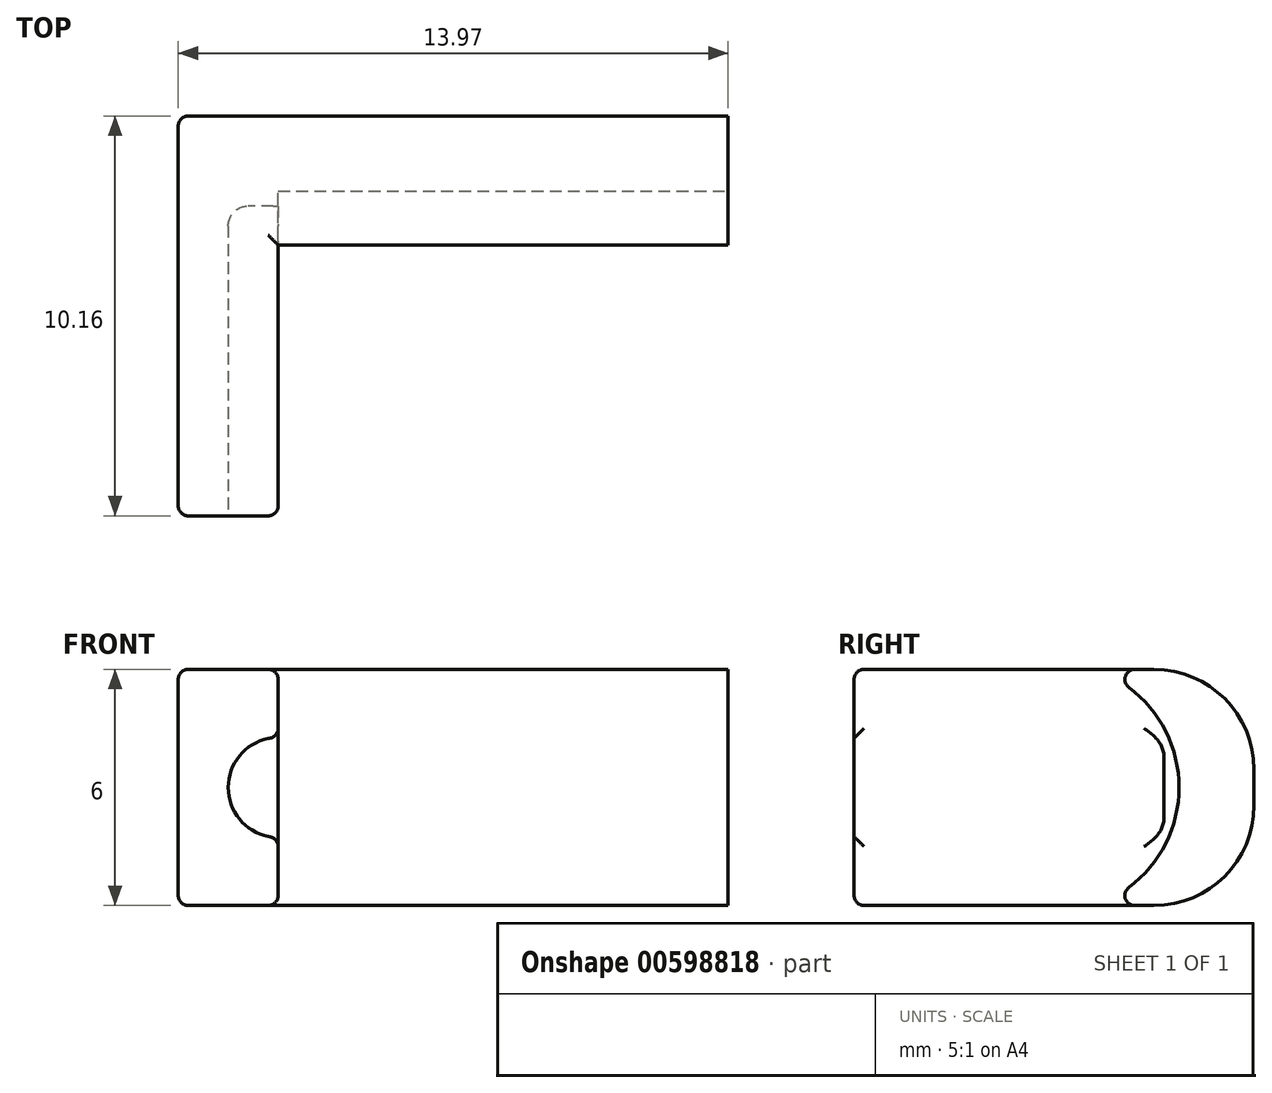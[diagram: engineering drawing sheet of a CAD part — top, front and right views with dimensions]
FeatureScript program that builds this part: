
annotation { "Feature Type Name" : "Feature", "Feature Type Description" : "" }
export const myFeature = defineFeature(function(context is Context, id is Id, definition is map)
    precondition{}
    {
        {
            var Q0;
            Q0=qCreatedBy(makeId("Top.planeOp"),FACE);
            var sketch = newSketch(context, id + "F0", { "sketchPlane" : qUnion([Q0])});
            skLineSegment(sketch, "E0", {"start": v(0, 0) * mm, "end": v(0, 0) * mm});
            skLineSegment(sketch, "E1.bottom", {"start": v(0, 0) * mm, "end": v(-13.97, 0) * mm});
            skLineSegment(sketch, "E1.top", {"start": v(0, -5.08) * mm, "end": v(-13.97, -5.08) * mm});
            skLineSegment(sketch, "E1.left", {"start": v(0, 0) * mm, "end": v(0, -5.08) * mm});
            skLineSegment(sketch, "E1.right", {"start": v(-13.97, 0) * mm, "end": v(-13.97, -5.08) * mm});
            skSolve(sketch);
        }
        {
            var Q0;
            Q0 = qSketchRegion(id + "F0", true);
            extrude(context, id + "F1", {"entities" : qUnion([Q0]), "depth" : 6 * mm, "offsetDistance" : 25.4 * mm});
        }
        {
            var Q0;
            Q0=makeQuery(id+"F1.opExtrude","SWEPT_FACE",FACE,{"disambiguationData":[OSD([sQuery(id+"F0.wireOp",EDGE,"E1.top")])]});
            var sketch = newSketch(context, id + "F2", { "sketchPlane" : qUnion([Q0])});
            skLineSegment(sketch, "E2.bottom", {"start": v(-13.97, 6) * mm, "end": v(-11.43, 6) * mm});
            skLineSegment(sketch, "E2.top", {"start": v(-13.97, 0) * mm, "end": v(-11.43, 0) * mm});
            skLineSegment(sketch, "E2.left", {"start": v(-13.97, 6) * mm, "end": v(-13.97, 0) * mm});
            skLineSegment(sketch, "E2.right", {"start": v(-11.43, 6) * mm, "end": v(-11.43, 1.76) * mm});
            skPoint(sketch, "E3.centerSnap0", {"position": v(-11.43, 3) * mm});
            skLineSegment(sketch, "E4.trimOffspring", {"start": v(-11.43, 1.76) * mm, "end": v(-11.43, 0) * mm});
            skSolve(sketch);
        }
        {
            var Q0;
            Q0 = qSketchRegion(id + "F2", true);
            extrude(context, id + "F3", {"entities" : qUnion([Q0]), "operationType" : NewBodyOperationType.ADD, "depth" : 5.08 * mm, "offsetDistance" : 25.4 * mm});
        }
        {
            var Q0;
            Q0=makeQuery(id+"F1.opExtrude","SWEPT_FACE",FACE,{"disambiguationData":[OSD([sQuery(id+"F0.wireOp",EDGE,"E1.left")])]});
            var sketch = newSketch(context, id + "F4", { "sketchPlane" : qUnion([Q0])});
            skCircle(sketch, "E5", {"center": v(-5.08, 3) * mm, "radius": 3.18 * mm});
            skSolve(sketch);
        }
        {
            var Q0;
            Q0 = qSketchRegion(id + "F4", true);
            extrude(context, id + "F5", {"entities" : qUnion([Q0]), "operationType" : NewBodyOperationType.REMOVE, "oppositeDirection" : true, "depth" : 11.43 * mm, "offsetDistance" : 25.4 * mm});
        }
        {
            var Q0;
            Q0=makeQuery(id+"F3.opExtrude","CAP_FACE",FACE,{"disambiguationData":[OSD([sQuery(id+"F2.wireOp",EDGE,"E2.bottom"),sQuery(id+"F2.wireOp",EDGE,"E2.top"),sQuery(id+"F2.wireOp",EDGE,"E2.left"),sQuery(id+"F2.wireOp",EDGE,"E2.right"),sQuery(id+"F2.wireOp",EDGE,"E4.trimOffspring")])],"isStart":false});
            var sketch = newSketch(context, id + "F6", { "sketchPlane" : qUnion([Q0])});
            skCircle(sketch, "E6", {"center": v(-11.43, 3) * mm, "radius": 1.27 * mm});
            skSolve(sketch);
        }
        {
            var Q0;
            Q0 = qSketchRegion(id + "F6", true);
            extrude(context, id + "F7", {"entities" : qUnion([Q0]), "operationType" : NewBodyOperationType.REMOVE, "oppositeDirection" : true, "depth" : 7.87 * mm, "offsetDistance" : 25.4 * mm});
        }
        {
            var Q0;
            Q0=makeQuery(id+"F1.opExtrude","CAP_EDGE",EDGE,{"disambiguationData":[OSD([sQuery(id+"F0.wireOp",EDGE,"E1.bottom")])],"isStart":false});
            var Q1;
            Q1=makeQuery(id+"F1.opExtrude","CAP_EDGE",EDGE,{"disambiguationData":[OSD([sQuery(id+"F0.wireOp",EDGE,"E1.bottom")])],"isStart":true});
            fillet(context, id + "F8", {"entities" : qUnion([Q0, Q1]), "radius" : 2.54 * mm, "tangentPropagation" : true, "allowEdgeOverflow" : false});
        }
        {
            var Q0;
            {var subQ0=sQuery(id+"F2.wireOp",EDGE,"E4.trimOffspring");var subQ1=sQuery(id+"F2.wireOp",EDGE,"E2.right");var subQ2=sQuery(id+"F2.wireOp",EDGE,"E2.bottom");Q0=makeQuery(id+"F7.boolean.opBoolean","SPLIT",EDGE,{"disambiguationData":[TD([makeQuery(id+"F3.opExtrude","SWEPT_FACE",FACE,{"disambiguationData":[OSD([subQ2])]})])],"derivedFrom":makeQuery(id+"F3.opExtrude","CAP_EDGE",EDGE,{"disambiguationData":[OSD([subQ1,subQ0])],"isStart":false})});}
            var Q1;
            Q1=makeQuery(id+"F3.opExtrude","CAP_EDGE",EDGE,{"disambiguationData":[OSD([sQuery(id+"F2.wireOp",EDGE,"E2.bottom")])],"isStart":false});
            var Q2;
            Q2=makeQuery(id+"F7.boolean.opBoolean","COPY",EDGE,{"derivedFrom":makeQuery(id+"F7.opExtrude","CAP_EDGE",EDGE,{"disambiguationData":[OSD([sQuery(id+"F6.wireOp",EDGE,"E6")])],"isStart":true})});
            var Q3;
            {var subQ0=sQuery(id+"F2.wireOp",EDGE,"E4.trimOffspring");var subQ1=sQuery(id+"F2.wireOp",EDGE,"E2.right");var subQ2=sQuery(id+"F2.wireOp",EDGE,"E2.top");Q3=makeQuery(id+"F7.boolean.opBoolean","SPLIT",EDGE,{"disambiguationData":[TD([makeQuery(id+"F3.opExtrude","SWEPT_FACE",FACE,{"disambiguationData":[OSD([subQ2])]})])],"derivedFrom":makeQuery(id+"F3.opExtrude","CAP_EDGE",EDGE,{"disambiguationData":[OSD([subQ1,subQ0])],"isStart":false})});}
            var Q4;
            Q4=makeQuery(id+"F3.opExtrude","CAP_EDGE",EDGE,{"disambiguationData":[OSD([sQuery(id+"F2.wireOp",EDGE,"E2.top")])],"isStart":false});
            var Q5;
            Q5=makeQuery(id+"F3.opExtrude","CAP_EDGE",EDGE,{"disambiguationData":[OSD([sQuery(id+"F2.wireOp",EDGE,"E2.left")])],"isStart":false});
            var Q6;
            Q6=makeQuery(id+"F3.boolean.opBoolean","MERGE",EDGE,{"derivedFrom":[makeQuery(id+"F1.opExtrude","CAP_EDGE",EDGE,{"disambiguationData":[OSD([sQuery(id+"F0.wireOp",EDGE,"E1.right")])],"isStart":false}),makeQuery(id+"F3.opExtrude","SWEPT_EDGE",EDGE,{"disambiguationData":[OSD([sQuery(id+"F2.wireOp",EDGE,"E2.bottom"),sQuery(id+"F2.wireOp",EDGE,"E2.left")])]})]});
            var Q7;
            Q7=makeQuery(id+"F5.boolean.opBoolean","INTERSECT",EDGE,{"derivedFrom":[makeQuery(id+"F3.boolean.opBoolean","MERGE",FACE,{"derivedFrom":[makeQuery(id+"F1.opExtrude","CAP_FACE",FACE,{"disambiguationData":[OSD([sQuery(id+"F0.wireOp",EDGE,"E1.bottom"),sQuery(id+"F0.wireOp",EDGE,"E1.top"),sQuery(id+"F0.wireOp",EDGE,"E1.left"),sQuery(id+"F0.wireOp",EDGE,"E1.right")])],"isStart":false}),makeQuery(id+"F3.opExtrude","SWEPT_FACE",FACE,{"disambiguationData":[OSD([sQuery(id+"F2.wireOp",EDGE,"E2.bottom")])]})]}),makeQuery(id+"F5.opExtrude","CAP_FACE",FACE,{"disambiguationData":[OSD([sQuery(id+"F4.wireOp",EDGE,"E5")])],"isStart":false})]});
            var Q8;
            Q8=makeQuery(id+"F5.boolean.opBoolean","INTERSECT",EDGE,{"derivedFrom":[makeQuery(id+"F3.boolean.opBoolean","MERGE",FACE,{"derivedFrom":[makeQuery(id+"F1.opExtrude","CAP_FACE",FACE,{"disambiguationData":[OSD([sQuery(id+"F0.wireOp",EDGE,"E1.bottom"),sQuery(id+"F0.wireOp",EDGE,"E1.top"),sQuery(id+"F0.wireOp",EDGE,"E1.left"),sQuery(id+"F0.wireOp",EDGE,"E1.right")])],"isStart":true}),makeQuery(id+"F3.opExtrude","SWEPT_FACE",FACE,{"disambiguationData":[OSD([sQuery(id+"F2.wireOp",EDGE,"E2.top")])]})]}),makeQuery(id+"F5.opExtrude","CAP_FACE",FACE,{"disambiguationData":[OSD([sQuery(id+"F4.wireOp",EDGE,"E5")])],"isStart":false})]});
            var Q9;
            Q9=makeQuery(id+"F7.boolean.opBoolean","INTERSECT",EDGE,{"disambiguationData":[OD(1.0)],"derivedFrom":[makeQuery(id+"F5.boolean.opBoolean","MERGE",FACE,{"derivedFrom":[makeQuery(id+"F3.opExtrude","SWEPT_FACE",FACE,{"disambiguationData":[OSD([sQuery(id+"F2.wireOp",EDGE,"E2.right"),sQuery(id+"F2.wireOp",EDGE,"E4.trimOffspring")])]}),makeQuery(id+"F5.opExtrude","CAP_FACE",FACE,{"disambiguationData":[OSD([sQuery(id+"F4.wireOp",EDGE,"E5")])],"isStart":false})]}),makeQuery(id+"F7.opExtrude","SWEPT_FACE",FACE,{"disambiguationData":[OSD([sQuery(id+"F6.wireOp",EDGE,"E6")])]})]});
            var Q10;
            Q10=makeQuery(id+"F7.boolean.opBoolean","INTERSECT",EDGE,{"disambiguationData":[OD(0.0)],"derivedFrom":[makeQuery(id+"F5.boolean.opBoolean","MERGE",FACE,{"derivedFrom":[makeQuery(id+"F3.opExtrude","SWEPT_FACE",FACE,{"disambiguationData":[OSD([sQuery(id+"F2.wireOp",EDGE,"E2.right"),sQuery(id+"F2.wireOp",EDGE,"E4.trimOffspring")])]}),makeQuery(id+"F5.opExtrude","CAP_FACE",FACE,{"disambiguationData":[OSD([sQuery(id+"F4.wireOp",EDGE,"E5")])],"isStart":false})]}),makeQuery(id+"F7.opExtrude","SWEPT_FACE",FACE,{"disambiguationData":[OSD([sQuery(id+"F6.wireOp",EDGE,"E6")])]})]});
            var Q11;
            Q11=makeQuery(id+"F5.boolean.opBoolean","INTERSECT",EDGE,{"derivedFrom":[makeQuery(id+"F3.boolean.opBoolean","MERGE",FACE,{"derivedFrom":[makeQuery(id+"F1.opExtrude","CAP_FACE",FACE,{"disambiguationData":[OSD([sQuery(id+"F0.wireOp",EDGE,"E1.bottom"),sQuery(id+"F0.wireOp",EDGE,"E1.top"),sQuery(id+"F0.wireOp",EDGE,"E1.left"),sQuery(id+"F0.wireOp",EDGE,"E1.right")])],"isStart":false}),makeQuery(id+"F3.opExtrude","SWEPT_FACE",FACE,{"disambiguationData":[OSD([sQuery(id+"F2.wireOp",EDGE,"E2.bottom")])]})]}),makeQuery(id+"F5.opExtrude","SWEPT_FACE",FACE,{"disambiguationData":[OSD([sQuery(id+"F4.wireOp",EDGE,"E5")])]})]});
            var Q12;
            Q12=makeQuery(id+"F5.boolean.opBoolean","INTERSECT",EDGE,{"derivedFrom":[makeQuery(id+"F3.boolean.opBoolean","MERGE",FACE,{"derivedFrom":[makeQuery(id+"F1.opExtrude","CAP_FACE",FACE,{"disambiguationData":[OSD([sQuery(id+"F0.wireOp",EDGE,"E1.bottom"),sQuery(id+"F0.wireOp",EDGE,"E1.top"),sQuery(id+"F0.wireOp",EDGE,"E1.left"),sQuery(id+"F0.wireOp",EDGE,"E1.right")])],"isStart":true}),makeQuery(id+"F3.opExtrude","SWEPT_FACE",FACE,{"disambiguationData":[OSD([sQuery(id+"F2.wireOp",EDGE,"E2.top")])]})]}),makeQuery(id+"F5.opExtrude","SWEPT_FACE",FACE,{"disambiguationData":[OSD([sQuery(id+"F4.wireOp",EDGE,"E5")])]})]});
            fillet(context, id + "F9", {"entities" : qUnion([Q0, Q1, Q2, Q3, Q4, Q5, Q6, Q7, Q8, Q9, Q10, Q11, Q12]), "radius" : 0.25 * mm, "tangentPropagation" : true, "allowEdgeOverflow" : false});
        }
        {
            var Q0;
            Q0=makeQuery(id+"F7.boolean.opBoolean","COPY",EDGE,{"derivedFrom":makeQuery(id+"F7.opExtrude","CAP_EDGE",EDGE,{"disambiguationData":[OSD([sQuery(id+"F6.wireOp",EDGE,"E6")])],"isStart":false})});
            fillet(context, id + "F10", {"entities" : qUnion([Q0]), "radius" : 0.5 * mm, "tangentPropagation" : true, "allowEdgeOverflow" : false});
        }
    });
